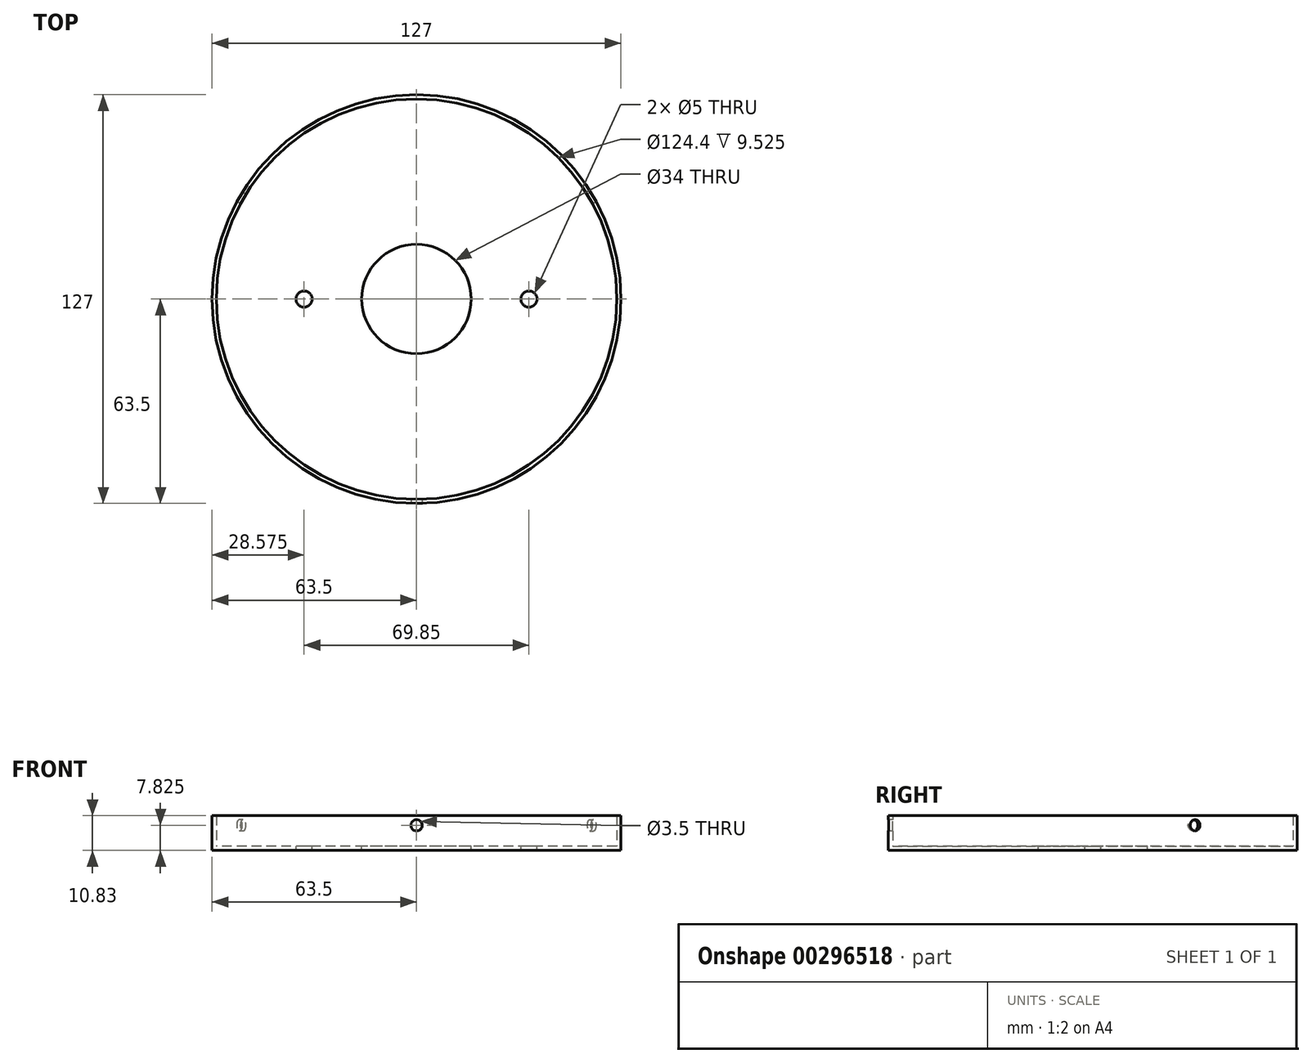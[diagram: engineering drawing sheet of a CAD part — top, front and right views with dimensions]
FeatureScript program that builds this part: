
annotation { "Feature Type Name" : "Feature", "Feature Type Description" : "" }
export const myFeature = defineFeature(function(context is Context, id is Id, definition is map)
    precondition{}
    {
        {
            var Q0;
            Q0=qCreatedBy(makeId("Top.planeOp"),FACE);
            var sketch = newSketch(context, id + "F0", { "sketchPlane" : qUnion([Q0])});
            skCircle(sketch, "E0", {"center": v(0, 0) * mm, "radius": 63.5 * mm});
            skSolve(sketch);
        }
        {
            var Q0;
            Q0 = qSketchRegion(id + "F0", true);
            extrude(context, id + "F1", {"entities" : qUnion([Q0]), "depth" : 1.3 * mm});
        }
        {
            var Q0;
            Q0=makeQuery(id+"F1.opExtrude","CAP_FACE",FACE,{"disambiguationData":[OSD([sQuery(id+"F0.wireOp",EDGE,"E0")])],"isStart":false});
            var sketch = newSketch(context, id + "F2", { "sketchPlane" : qUnion([Q0])});
            skCircle(sketch, "E1", {"center": v(-34.93, 0) * mm, "radius": 2.5 * mm});
            skCircle(sketch, "E2", {"center": v(34.93, 0) * mm, "radius": 2.5 * mm});
            skLineSegment(sketch, "E3", {"start": v(-34.93, 0) * mm, "end": v(34.93, 0) * mm, "construction": true});
            skSolve(sketch);
        }
        {
            var Q0;
            Q0 = qSketchRegion(id + "F2", true);
            extrude(context, id + "F3", {"entities" : qUnion([Q0]), "operationType" : NewBodyOperationType.REMOVE, "oppositeDirection" : true, "depth" : 25 * mm});
        }
        {
            var Q0;
            Q0=makeQuery(id+"F1.opExtrude","CAP_FACE",FACE,{"disambiguationData":[OSD([sQuery(id+"F0.wireOp",EDGE,"E0")])],"isStart":false});
            var sketch = newSketch(context, id + "F4", { "sketchPlane" : qUnion([Q0])});
            skCircle(sketch, "E4.0", {"center": v(0, 0) * mm, "radius": 63.5 * mm});
            skCircle(sketch, "E5.0", {"center": v(0, 0) * mm, "radius": 62.2 * mm});
            skSolve(sketch);
        }
        {
            var Q0;
            Q0 = qSketchRegion(id + "F4", true);
            extrude(context, id + "F5", {"entities" : qUnion([Q0]), "operationType" : NewBodyOperationType.ADD, "depth" : 9.52 * mm});
        }
        {
            var Q0;
            Q0=qCreatedBy(makeId("Front.planeOp"),FACE);
            cPlane(context, id + "F6", {"entities" : qUnion([Q0]), "cplaneType" : CPlaneType.OFFSET, "offset" : 63.9 * mm, "width" : 150 * mm, "height" : 150 * mm});
        }
        {
            var Q0;
            Q0=qCreatedBy(id+"F6.planeOp",FACE);
            var sketch = newSketch(context, id + "F7", { "sketchPlane" : qUnion([Q0])});
            skCircle(sketch, "E6", {"center": v(0, 7.83) * mm, "radius": 1.75 * mm});
            skSolve(sketch);
        }
        {
            var Q0;
            Q0 = qSketchRegion(id + "F7", true);
            var Q1;
            Q1=makeQuery(id+"F5.opExtrude","SWEPT_FACE",FACE,{"disambiguationData":[OSD([sQuery(id+"F4.wireOp",EDGE,"E5.0")])]});
            extrude(context, id + "F8", {"entities" : qUnion([Q0]), "oppositeDirection" : true, "endBoundEntityFace" : qUnion([Q1]), "depth" : 5 * mm});
        }
        {
            var Q0;
            Q0=makeQuery(id+"F8.opExtrude","SWEPT_BODY",BODY,{"disambiguationData":[OSD([sQuery(id+"F7.wireOp",EDGE,"E6")])]});
            var Q1;
            Q1=makeQuery(id+"F5.boolean.opBoolean","MERGE",FACE,{"derivedFrom":[makeQuery(id+"F1.opExtrude","SWEPT_FACE",FACE,{"disambiguationData":[OSD([sQuery(id+"F0.wireOp",EDGE,"E0")])]}),makeQuery(id+"F5.opExtrude","SWEPT_FACE",FACE,{"disambiguationData":[OSD([sQuery(id+"F4.wireOp",EDGE,"E4.0")])]})]});
            circularPattern(context, id + "F9", {"entities" : qUnion([Q0]), "axis" : qUnion([Q1]), "angle" : 360 * degree, "instanceCount" : 3, "equalSpace" : true});
        }
        {
            var Q0;
            Q0=makeQuery(id+"F8.opExtrude","SWEPT_BODY",BODY,{"disambiguationData":[OSD([sQuery(id+"F7.wireOp",EDGE,"E6")])]});
            var Q1;
            Q1=makeQuery(id+"F9.opPattern","COPY",BODY,{"derivedFrom":makeQuery(id+"F8.opExtrude","SWEPT_BODY",BODY,{"disambiguationData":[OSD([sQuery(id+"F7.wireOp",EDGE,"E6")])]}),"instanceName":"2"});
            var Q2;
            Q2=makeQuery(id+"F9.opPattern","COPY",BODY,{"derivedFrom":makeQuery(id+"F8.opExtrude","SWEPT_BODY",BODY,{"disambiguationData":[OSD([sQuery(id+"F7.wireOp",EDGE,"E6")])]}),"instanceName":"1"});
            var Q3;
            Q3=makeQuery(id+"F1.opExtrude","SWEPT_BODY",BODY,{"disambiguationData":[OSD([sQuery(id+"F0.wireOp",EDGE,"E0")])]});
            booleanBodies(context, id + "F10", {"operationType" : BooleanOperationType.SUBTRACTION, "tools" : qUnion([Q0, Q1, Q2]), "targets" : qUnion([Q3])});
        }
        {
            var Q0;
            Q0=makeQuery(id+"F1.opExtrude","CAP_FACE",FACE,{"disambiguationData":[OSD([sQuery(id+"F0.wireOp",EDGE,"E0")])],"isStart":false});
            var sketch = newSketch(context, id + "F11", { "sketchPlane" : qUnion([Q0])});
            skCircle(sketch, "E7", {"center": v(0, 0) * mm, "radius": 17 * mm});
            skSolve(sketch);
        }
        {
            var Q0;
            Q0 = qSketchRegion(id + "F11", true);
            extrude(context, id + "F12", {"entities" : qUnion([Q0]), "operationType" : NewBodyOperationType.REMOVE, "oppositeDirection" : true, "depth" : 25 * mm});
        }
    });
